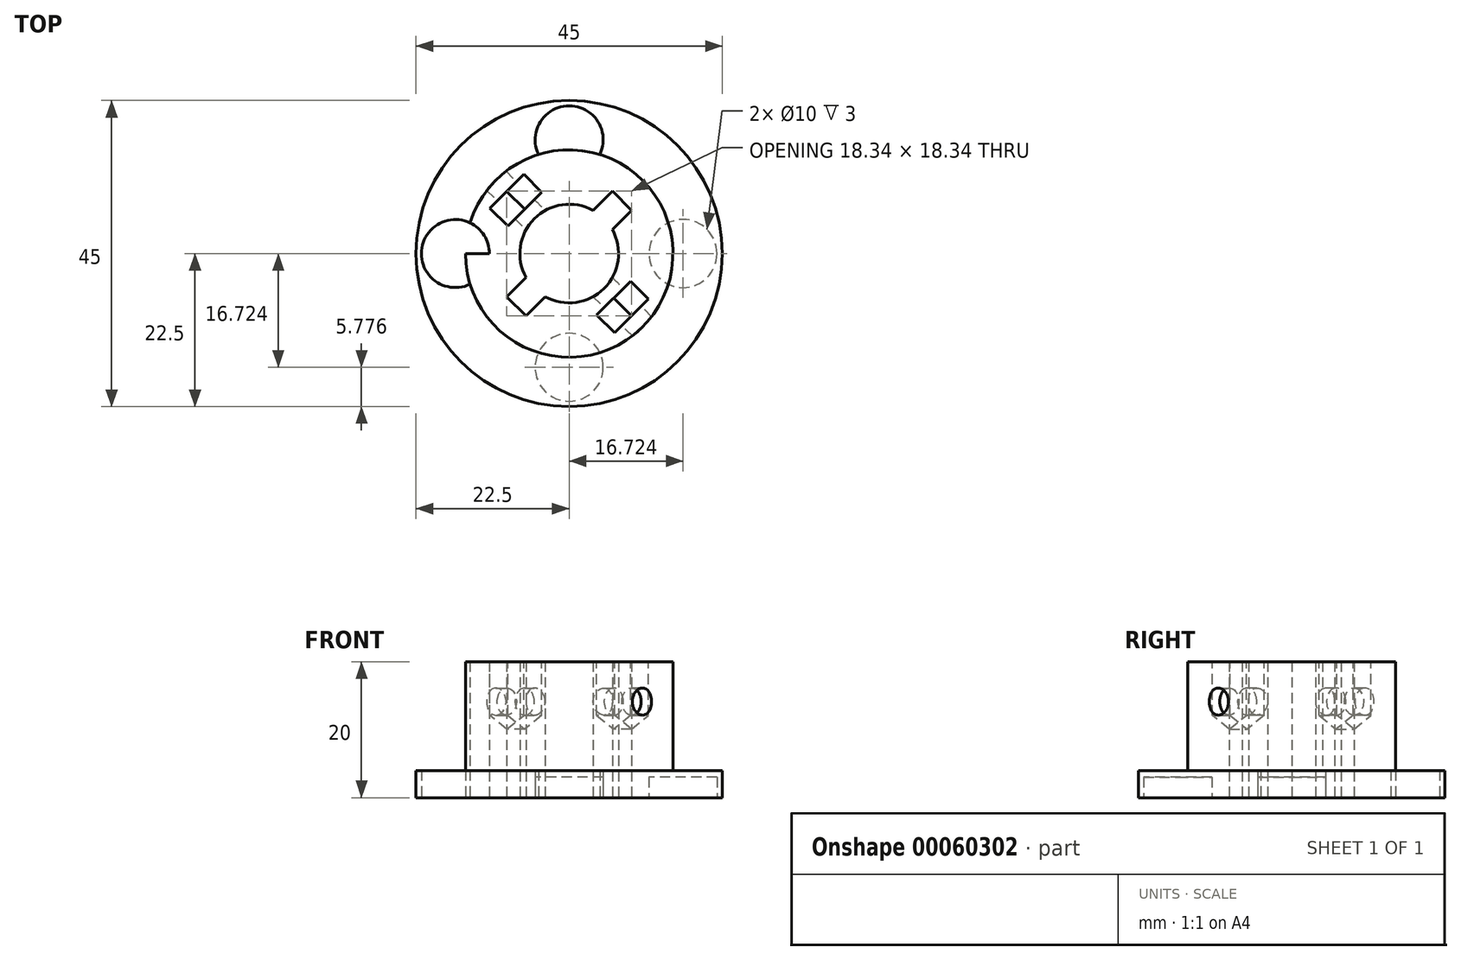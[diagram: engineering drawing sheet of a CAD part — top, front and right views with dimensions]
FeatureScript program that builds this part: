
annotation { "Feature Type Name" : "Feature", "Feature Type Description" : "" }
export const myFeature = defineFeature(function(context is Context, id is Id, definition is map)
    precondition{}
    {
        {
            var Q0;
            Q0=qCreatedBy(makeId("Top.planeOp"),FACE);
            var sketch = newSketch(context, id + "F0", { "sketchPlane" : qUnion([Q0])});
            skCircle(sketch, "E0", {"center": v(0, 0) * mm, "radius": 22.5 * mm});
            skLineSegment(sketch, "E1", {"start": v(0, 22.5) * mm, "end": v(0, -22.5) * mm});
            skLineSegment(sketch, "E2", {"start": v(-22.5, 0) * mm, "end": v(22.5, 0) * mm});
            skCircle(sketch, "E3", {"center": v(0, 0) * mm, "radius": 7.25 * mm});
            skCircle(sketch, "E4", {"center": v(0, 0) * mm, "radius": 15.25 * mm});
            skCircle(sketch, "E5", {"center": v(0, -16.72) * mm, "radius": 5 * mm});
            skLineSegment(sketch, "E6", {"start": v(-15.9, -15.9) * mm, "end": v(15.9, 15.9) * mm});
            skCircle(sketch, "E7.MirrorC", {"center": v(0, 16.72) * mm, "radius": 5 * mm});
            skCircle(sketch, "E8.MirrorC", {"center": v(-16.72, 0) * mm, "radius": 5 * mm});
            skCircle(sketch, "E9.MirrorC", {"center": v(16.72, 0) * mm, "radius": 5 * mm});
            skLineSegment(sketch, "E10", {"start": v(-6.34, -3.51) * mm, "end": v(-9.17, -6.34) * mm});
            skLineSegment(sketch, "E11", {"start": v(-9.17, -6.34) * mm, "end": v(-6.34, -9.17) * mm});
            skLineSegment(sketch, "E12", {"start": v(-6.34, -9.17) * mm, "end": v(-3.51, -6.34) * mm});
            skLineSegment(sketch, "E13", {"start": v(-15.9, 15.9) * mm, "end": v(15.9, -15.9) * mm, "construction": true});
            skLineSegment(sketch, "E14.MirrorCS", {"start": v(3.51, 6.34) * mm, "end": v(6.34, 9.17) * mm});
            skLineSegment(sketch, "E15.MirrorCS", {"start": v(6.34, 9.17) * mm, "end": v(9.17, 6.34) * mm});
            skLineSegment(sketch, "E16.MirrorCS", {"start": v(9.17, 6.34) * mm, "end": v(6.34, 3.51) * mm});
            skSolve(sketch);
        }
        {
            var Q0;
            {var subQ0=sQuery(id+"F0.wireOp",EDGE,"E4");var subQ1=sQuery(id+"F0.wireOp",EDGE,"E1");var subQ2=makeQuery(id+"F0.imprint","INTERSECT",VERTEX,{"disambiguationData":[OD(0.0)],"derivedFrom":[subQ1,subQ0]});Q0=makeQuery(id+"F0.imprint","IMPRINT",FACE,{"disambiguationData":[TD([[makeQuery(id+"F0.imprint","IMPRINT",EDGE,{"disambiguationData":[TD([[subQ2,-1.0]])],"derivedFrom":subQ1}),-1.0]])]});}
            var Q1;
            {var subQ0=sQuery(id+"F0.wireOp",EDGE,"E4");var subQ1=sQuery(id+"F0.wireOp",EDGE,"E1");var subQ2=makeQuery(id+"F0.imprint","INTERSECT",VERTEX,{"disambiguationData":[OD(0.0)],"derivedFrom":[subQ1,subQ0]});Q1=makeQuery(id+"F0.imprint","IMPRINT",FACE,{"disambiguationData":[TD([[makeQuery(id+"F0.imprint","IMPRINT",EDGE,{"disambiguationData":[TD([[subQ2,-1.0]])],"derivedFrom":subQ1}),1.0]])]});}
            var Q2;
            {var subQ5=sQuery(id+"F0.wireOp",EDGE,"E2");var subQ8=sQuery(id+"F0.wireOp",EDGE,"E3");var subQ9=makeQuery(id+"F0.imprint","INTERSECT",VERTEX,{"disambiguationData":[OD(1.0)],"derivedFrom":[subQ5,subQ8]});Q2=makeQuery(id+"F0.imprint","IMPRINT",FACE,{"disambiguationData":[TD([[makeQuery(id+"F0.imprint","IMPRINT",EDGE,{"disambiguationData":[TD([[subQ9,-1.0]])],"derivedFrom":subQ5}),1.0]])]});}
            var Q3;
            {var subQ0=sQuery(id+"F0.wireOp",EDGE,"E3");var subQ1=sQuery(id+"F0.wireOp",EDGE,"E1");var subQ2=makeQuery(id+"F0.imprint","INTERSECT",VERTEX,{"disambiguationData":[OD(1.0)],"derivedFrom":[subQ1,subQ0]});Q3=makeQuery(id+"F0.imprint","IMPRINT",FACE,{"disambiguationData":[TD([[makeQuery(id+"F0.imprint","IMPRINT",EDGE,{"disambiguationData":[TD([[subQ2,-1.0]])],"derivedFrom":subQ1}),1.0]])]});}
            var Q4;
            {var subQ6=sQuery(id+"F0.wireOp",EDGE,"E3");var subQ7=sQuery(id+"F0.wireOp",EDGE,"E1");var subQ8=makeQuery(id+"F0.imprint","INTERSECT",VERTEX,{"disambiguationData":[OD(1.0)],"derivedFrom":[subQ7,subQ6]});Q4=makeQuery(id+"F0.imprint","IMPRINT",FACE,{"disambiguationData":[TD([[makeQuery(id+"F0.imprint","IMPRINT",EDGE,{"disambiguationData":[TD([[subQ8,-1.0]])],"derivedFrom":subQ7}),-1.0]])]});}
            var Q5;
            {var subQ1=sQuery(id+"F0.wireOp",EDGE,"E4");var subQ5=sQuery(id+"F0.wireOp",EDGE,"E2");var subQ6=makeQuery(id+"F0.imprint","INTERSECT",VERTEX,{"disambiguationData":[OD(0.0)],"derivedFrom":[subQ5,subQ1]});Q5=makeQuery(id+"F0.imprint","IMPRINT",FACE,{"disambiguationData":[TD([[makeQuery(id+"F0.imprint","IMPRINT",EDGE,{"disambiguationData":[TD([[subQ6,-1.0]])],"derivedFrom":subQ5}),-1.0]])]});}
            var Q6;
            {var subQ0=sQuery(id+"F0.wireOp",EDGE,"1c631775-3706-4f81-9fae-aeb5620db3840.MirrorC");var subQ1=sQuery(id+"F0.wireOp",EDGE,"E4");var subQ2=makeQuery(id+"F0.imprint","INTERSECT",VERTEX,{"disambiguationData":[OD(0.0)],"derivedFrom":[subQ1,subQ0]});Q6=makeQuery(id+"F0.imprint","IMPRINT",FACE,{"disambiguationData":[TD([[makeQuery(id+"F0.imprint","IMPRINT",EDGE,{"disambiguationData":[TD([[subQ2,-1.0]])],"derivedFrom":subQ1}),1.0]])]});}
            var Q7;
            {var subQ0=sQuery(id+"F0.wireOp",EDGE,"60ae7ea0-6620-475c-871b-af027508dd5f0.MirrorC");var subQ1=sQuery(id+"F0.wireOp",EDGE,"E4");var subQ2=makeQuery(id+"F0.imprint","INTERSECT",VERTEX,{"disambiguationData":[OD(0.0)],"derivedFrom":[subQ1,subQ0]});Q7=makeQuery(id+"F0.imprint","IMPRINT",FACE,{"disambiguationData":[TD([[makeQuery(id+"F0.imprint","IMPRINT",EDGE,{"disambiguationData":[TD([[subQ2,-1.0]])],"derivedFrom":subQ1}),1.0]])]});}
            var Q8;
            {var subQ0=sQuery(id+"F0.wireOp",EDGE,"c14ca91b-31c8-40ef-a71a-b8f91e1f63390.MirrorC");var subQ1=sQuery(id+"F0.wireOp",EDGE,"E4");var subQ2=makeQuery(id+"F0.imprint","INTERSECT",VERTEX,{"disambiguationData":[OD(0.0)],"derivedFrom":[subQ1,subQ0]});Q8=makeQuery(id+"F0.imprint","IMPRINT",FACE,{"disambiguationData":[TD([[makeQuery(id+"F0.imprint","IMPRINT",EDGE,{"disambiguationData":[TD([[subQ2,-1.0]])],"derivedFrom":subQ1}),1.0]])]});}
            var Q9;
            {var subQ0=sQuery(id+"F0.wireOp",EDGE,"be21c227-3566-4778-a96a-078e8c0b7c8a0.MirrorC");var subQ1=sQuery(id+"F0.wireOp",EDGE,"E4");var subQ2=makeQuery(id+"F0.imprint","INTERSECT",VERTEX,{"disambiguationData":[OD(0.0)],"derivedFrom":[subQ1,subQ0]});Q9=makeQuery(id+"F0.imprint","IMPRINT",FACE,{"disambiguationData":[TD([[makeQuery(id+"F0.imprint","IMPRINT",EDGE,{"disambiguationData":[TD([[subQ2,-1.0]])],"derivedFrom":subQ1}),1.0]])]});}
            var Q10;
            {var subQ0=sQuery(id+"F0.wireOp",EDGE,"ab68310c-7daf-4449-9c12-ef71371e41db0.MirrorC");var subQ1=sQuery(id+"F0.wireOp",EDGE,"E4");var subQ2=makeQuery(id+"F0.imprint","INTERSECT",VERTEX,{"disambiguationData":[OD(0.0)],"derivedFrom":[subQ1,subQ0]});Q10=makeQuery(id+"F0.imprint","IMPRINT",FACE,{"disambiguationData":[TD([[makeQuery(id+"F0.imprint","IMPRINT",EDGE,{"disambiguationData":[TD([[subQ2,-1.0]])],"derivedFrom":subQ1}),1.0]])]});}
            var Q11;
            {var subQ0=sQuery(id+"F0.wireOp",EDGE,"E5");var subQ1=sQuery(id+"F0.wireOp",EDGE,"E4");var subQ2=makeQuery(id+"F0.imprint","INTERSECT",VERTEX,{"disambiguationData":[OD(0.0)],"derivedFrom":[subQ1,subQ0]});Q11=makeQuery(id+"F0.imprint","IMPRINT",FACE,{"disambiguationData":[TD([[makeQuery(id+"F0.imprint","IMPRINT",EDGE,{"disambiguationData":[TD([[subQ2,-1.0]])],"derivedFrom":subQ1}),1.0]])]});}
            var Q12;
            {var subQ0=sQuery(id+"F0.wireOp",EDGE,"a2d47717-2f6c-4d2c-92b3-d8f29983befe0.MirrorC");var subQ1=sQuery(id+"F0.wireOp",EDGE,"E4");var subQ2=makeQuery(id+"F0.imprint","INTERSECT",VERTEX,{"disambiguationData":[OD(0.0)],"derivedFrom":[subQ1,subQ0]});Q12=makeQuery(id+"F0.imprint","IMPRINT",FACE,{"disambiguationData":[TD([[makeQuery(id+"F0.imprint","IMPRINT",EDGE,{"disambiguationData":[TD([[subQ2,-1.0]])],"derivedFrom":subQ1}),1.0]])]});}
            var Q13;
            {var subQ0=sQuery(id+"F0.wireOp",EDGE,"ad0277b0-81cc-4cec-893f-fa6e84c42cf90.MirrorC");var subQ1=sQuery(id+"F0.wireOp",EDGE,"E4");var subQ2=makeQuery(id+"F0.imprint","INTERSECT",VERTEX,{"disambiguationData":[OD(0.0)],"derivedFrom":[subQ1,subQ0]});Q13=makeQuery(id+"F0.imprint","IMPRINT",FACE,{"disambiguationData":[TD([[makeQuery(id+"F0.imprint","IMPRINT",EDGE,{"disambiguationData":[TD([[subQ2,-1.0]])],"derivedFrom":subQ1}),1.0]])]});}
            var Q14;
            {var subQ0=sQuery(id+"F0.wireOp",EDGE,"E8.MirrorC");var subQ6=sQuery(id+"F0.wireOp",EDGE,"E2");var subQ9=makeQuery(id+"F0.imprint","INTERSECT",VERTEX,{"disambiguationData":[OD(1.0)],"derivedFrom":[subQ6,subQ0]});Q14=makeQuery(id+"F0.imprint","IMPRINT",FACE,{"disambiguationData":[TD([[makeQuery(id+"F0.imprint","IMPRINT",EDGE,{"disambiguationData":[TD([[subQ9,-1.0]])],"derivedFrom":subQ6}),-1.0]])]});}
            var Q15;
            {var subQ0=sQuery(id+"F0.wireOp",EDGE,"E5");var subQ1=sQuery(id+"F0.wireOp",EDGE,"E1");var subQ2=makeQuery(id+"F0.imprint","INTERSECT",VERTEX,{"disambiguationData":[OD(0.0)],"derivedFrom":[subQ1,subQ0]});Q15=makeQuery(id+"F0.imprint","IMPRINT",FACE,{"disambiguationData":[TD([[makeQuery(id+"F0.imprint","IMPRINT",EDGE,{"disambiguationData":[TD([[subQ2,-1.0]])],"derivedFrom":subQ1}),1.0]])]});}
            var Q16;
            {var subQ1=sQuery(id+"F0.wireOp",EDGE,"E1");var subQ5=sQuery(id+"F0.wireOp",EDGE,"E7.MirrorC");var subQ11=makeQuery(id+"F0.imprint","INTERSECT",VERTEX,{"disambiguationData":[OD(1.0)],"derivedFrom":[subQ1,subQ5]});Q16=makeQuery(id+"F0.imprint","IMPRINT",FACE,{"disambiguationData":[TD([[makeQuery(id+"F0.imprint","IMPRINT",EDGE,{"disambiguationData":[TD([[subQ11,-1.0]])],"derivedFrom":subQ1}),-1.0]])]});}
            var Q17;
            {var subQ5=sQuery(id+"F0.wireOp",EDGE,"E7.MirrorC");var subQ6=sQuery(id+"F0.wireOp",EDGE,"E1");var subQ7=makeQuery(id+"F0.imprint","INTERSECT",VERTEX,{"disambiguationData":[OD(1.0)],"derivedFrom":[subQ6,subQ5]});Q17=makeQuery(id+"F0.imprint","IMPRINT",FACE,{"disambiguationData":[TD([[makeQuery(id+"F0.imprint","IMPRINT",EDGE,{"disambiguationData":[TD([[subQ7,-1.0]])],"derivedFrom":subQ6}),1.0]])]});}
            var Q18;
            {var subQ0=sQuery(id+"F0.wireOp",EDGE,"E9.MirrorC");var subQ1=sQuery(id+"F0.wireOp",EDGE,"E2");var subQ2=makeQuery(id+"F0.imprint","INTERSECT",VERTEX,{"disambiguationData":[OD(0.0)],"derivedFrom":[subQ1,subQ0]});Q18=makeQuery(id+"F0.imprint","IMPRINT",FACE,{"disambiguationData":[TD([[makeQuery(id+"F0.imprint","IMPRINT",EDGE,{"disambiguationData":[TD([[subQ2,-1.0]])],"derivedFrom":subQ1}),1.0]])]});}
            var Q19;
            {var subQ0=sQuery(id+"F0.wireOp",EDGE,"E9.MirrorC");var subQ1=sQuery(id+"F0.wireOp",EDGE,"E2");var subQ2=makeQuery(id+"F0.imprint","INTERSECT",VERTEX,{"disambiguationData":[OD(0.0)],"derivedFrom":[subQ1,subQ0]});Q19=makeQuery(id+"F0.imprint","IMPRINT",FACE,{"disambiguationData":[TD([[makeQuery(id+"F0.imprint","IMPRINT",EDGE,{"disambiguationData":[TD([[subQ2,-1.0]])],"derivedFrom":subQ1}),-1.0]])]});}
            extrude(context, id + "F1", {"entities" : qUnion([Q0, Q1, Q2, Q3, Q4, Q5, Q6, Q7, Q8, Q9, Q10, Q11, Q12, Q13, Q14, Q15, Q16, Q17, Q18, Q19]), "depth" : 20 * mm});
        }
        {
            var Q0;
            {var subQ1=sQuery(id+"F0.wireOp",EDGE,"E0");var subQ5=sQuery(id+"F0.wireOp",EDGE,"E1");var subQ9=makeQuery(id+"F0.imprint","INTERSECT",VERTEX,{"disambiguationData":[OD(1.0)],"derivedFrom":[subQ1,subQ5]});Q0=makeQuery(id+"F0.imprint","IMPRINT",FACE,{"disambiguationData":[TD([[makeQuery(id+"F0.imprint","IMPRINT",EDGE,{"disambiguationData":[TD([[subQ9,-1.0]])],"derivedFrom":subQ1}),1.0]])]});}
            var Q1;
            {var subQ0=sQuery(id+"F0.wireOp",EDGE,"ab68310c-7daf-4449-9c12-ef71371e41db0.MirrorC");var subQ1=sQuery(id+"F0.wireOp",EDGE,"E4");var subQ2=makeQuery(id+"F0.imprint","INTERSECT",VERTEX,{"disambiguationData":[OD(0.0)],"derivedFrom":[subQ1,subQ0]});Q1=makeQuery(id+"F0.imprint","IMPRINT",FACE,{"disambiguationData":[TD([[makeQuery(id+"F0.imprint","IMPRINT",EDGE,{"disambiguationData":[TD([[subQ2,-1.0]])],"derivedFrom":subQ1}),-1.0]])]});}
            var Q2;
            {var subQ5=sQuery(id+"F0.wireOp",EDGE,"E2");var subQ8=sQuery(id+"F0.wireOp",EDGE,"E0");var subQ9=makeQuery(id+"F0.imprint","INTERSECT",VERTEX,{"disambiguationData":[OD(1.0)],"derivedFrom":[subQ8,subQ5]});Q2=makeQuery(id+"F0.imprint","IMPRINT",FACE,{"disambiguationData":[TD([[makeQuery(id+"F0.imprint","IMPRINT",EDGE,{"disambiguationData":[TD([[subQ9,-1.0]])],"derivedFrom":subQ8}),1.0]])]});}
            var Q3;
            {var subQ0=sQuery(id+"F0.wireOp",EDGE,"be21c227-3566-4778-a96a-078e8c0b7c8a0.MirrorC");var subQ1=sQuery(id+"F0.wireOp",EDGE,"E4");var subQ2=makeQuery(id+"F0.imprint","INTERSECT",VERTEX,{"disambiguationData":[OD(0.0)],"derivedFrom":[subQ1,subQ0]});Q3=makeQuery(id+"F0.imprint","IMPRINT",FACE,{"disambiguationData":[TD([[makeQuery(id+"F0.imprint","IMPRINT",EDGE,{"disambiguationData":[TD([[subQ2,-1.0]])],"derivedFrom":subQ1}),-1.0]])]});}
            var Q4;
            {var subQ0=sQuery(id+"F0.wireOp",EDGE,"E5");var subQ1=sQuery(id+"F0.wireOp",EDGE,"E4");var subQ2=makeQuery(id+"F0.imprint","INTERSECT",VERTEX,{"disambiguationData":[OD(0.0)],"derivedFrom":[subQ1,subQ0]});Q4=makeQuery(id+"F0.imprint","IMPRINT",FACE,{"disambiguationData":[TD([[makeQuery(id+"F0.imprint","IMPRINT",EDGE,{"disambiguationData":[TD([[subQ2,-1.0]])],"derivedFrom":subQ1}),-1.0]])]});}
            var Q5;
            {var subQ5=sQuery(id+"F0.wireOp",EDGE,"E1");var subQ8=sQuery(id+"F0.wireOp",EDGE,"E0");var subQ10=makeQuery(id+"F0.imprint","INTERSECT",VERTEX,{"disambiguationData":[OD(1.0)],"derivedFrom":[subQ8,subQ5]});Q5=makeQuery(id+"F0.imprint","IMPRINT",FACE,{"disambiguationData":[TD([[makeQuery(id+"F0.imprint","IMPRINT",EDGE,{"disambiguationData":[TD([[subQ10,1.0]])],"derivedFrom":subQ8}),1.0]])]});}
            var Q6;
            {var subQ0=sQuery(id+"F0.wireOp",EDGE,"a2d47717-2f6c-4d2c-92b3-d8f29983befe0.MirrorC");var subQ1=sQuery(id+"F0.wireOp",EDGE,"E4");var subQ2=makeQuery(id+"F0.imprint","INTERSECT",VERTEX,{"disambiguationData":[OD(0.0)],"derivedFrom":[subQ1,subQ0]});Q6=makeQuery(id+"F0.imprint","IMPRINT",FACE,{"disambiguationData":[TD([[makeQuery(id+"F0.imprint","IMPRINT",EDGE,{"disambiguationData":[TD([[subQ2,-1.0]])],"derivedFrom":subQ1}),-1.0]])]});}
            var Q7;
            {var subQ5=sQuery(id+"F0.wireOp",EDGE,"E2");var subQ8=sQuery(id+"F0.wireOp",EDGE,"E0");var subQ9=makeQuery(id+"F0.imprint","INTERSECT",VERTEX,{"disambiguationData":[OD(0.0)],"derivedFrom":[subQ8,subQ5]});Q7=makeQuery(id+"F0.imprint","IMPRINT",FACE,{"disambiguationData":[TD([[makeQuery(id+"F0.imprint","IMPRINT",EDGE,{"disambiguationData":[TD([[subQ9,-1.0]])],"derivedFrom":subQ8}),1.0]])]});}
            var Q8;
            {var subQ0=sQuery(id+"F0.wireOp",EDGE,"ad0277b0-81cc-4cec-893f-fa6e84c42cf90.MirrorC");var subQ1=sQuery(id+"F0.wireOp",EDGE,"E4");var subQ2=makeQuery(id+"F0.imprint","INTERSECT",VERTEX,{"disambiguationData":[OD(0.0)],"derivedFrom":[subQ1,subQ0]});Q8=makeQuery(id+"F0.imprint","IMPRINT",FACE,{"disambiguationData":[TD([[makeQuery(id+"F0.imprint","IMPRINT",EDGE,{"disambiguationData":[TD([[subQ2,-1.0]])],"derivedFrom":subQ1}),-1.0]])]});}
            var Q9;
            {var subQ0=sQuery(id+"F0.wireOp",EDGE,"1c631775-3706-4f81-9fae-aeb5620db3840.MirrorC");var subQ1=sQuery(id+"F0.wireOp",EDGE,"E4");var subQ2=makeQuery(id+"F0.imprint","INTERSECT",VERTEX,{"disambiguationData":[OD(0.0)],"derivedFrom":[subQ1,subQ0]});Q9=makeQuery(id+"F0.imprint","IMPRINT",FACE,{"disambiguationData":[TD([[makeQuery(id+"F0.imprint","IMPRINT",EDGE,{"disambiguationData":[TD([[subQ2,-1.0]])],"derivedFrom":subQ1}),-1.0]])]});}
            var Q10;
            {var subQ1=sQuery(id+"F0.wireOp",EDGE,"E1");var subQ6=sQuery(id+"F0.wireOp",EDGE,"E0");var subQ9=makeQuery(id+"F0.imprint","INTERSECT",VERTEX,{"disambiguationData":[OD(0.0)],"derivedFrom":[subQ6,subQ1]});Q10=makeQuery(id+"F0.imprint","IMPRINT",FACE,{"disambiguationData":[TD([[makeQuery(id+"F0.imprint","IMPRINT",EDGE,{"disambiguationData":[TD([[subQ9,-1.0]])],"derivedFrom":subQ6}),1.0]])]});}
            var Q11;
            {var subQ0=sQuery(id+"F0.wireOp",EDGE,"60ae7ea0-6620-475c-871b-af027508dd5f0.MirrorC");var subQ1=sQuery(id+"F0.wireOp",EDGE,"E4");var subQ2=makeQuery(id+"F0.imprint","INTERSECT",VERTEX,{"disambiguationData":[OD(0.0)],"derivedFrom":[subQ1,subQ0]});Q11=makeQuery(id+"F0.imprint","IMPRINT",FACE,{"disambiguationData":[TD([[makeQuery(id+"F0.imprint","IMPRINT",EDGE,{"disambiguationData":[TD([[subQ2,-1.0]])],"derivedFrom":subQ1}),-1.0]])]});}
            var Q12;
            {var subQ0=sQuery(id+"F0.wireOp",EDGE,"c14ca91b-31c8-40ef-a71a-b8f91e1f63390.MirrorC");var subQ1=sQuery(id+"F0.wireOp",EDGE,"E4");var subQ2=makeQuery(id+"F0.imprint","INTERSECT",VERTEX,{"disambiguationData":[OD(0.0)],"derivedFrom":[subQ1,subQ0]});Q12=makeQuery(id+"F0.imprint","IMPRINT",FACE,{"disambiguationData":[TD([[makeQuery(id+"F0.imprint","IMPRINT",EDGE,{"disambiguationData":[TD([[subQ2,-1.0]])],"derivedFrom":subQ1}),-1.0]])]});}
            var Q13;
            {var subQ1=sQuery(id+"F0.wireOp",EDGE,"E1");var subQ8=sQuery(id+"F0.wireOp",EDGE,"E0");var subQ9=makeQuery(id+"F0.imprint","INTERSECT",VERTEX,{"disambiguationData":[OD(0.0)],"derivedFrom":[subQ8,subQ1]});Q13=makeQuery(id+"F0.imprint","IMPRINT",FACE,{"disambiguationData":[TD([[makeQuery(id+"F0.imprint","IMPRINT",EDGE,{"disambiguationData":[TD([[subQ9,1.0]])],"derivedFrom":subQ8}),1.0]])]});}
            var Q14;
            {var subQ0=sQuery(id+"F0.wireOp",EDGE,"E4");var subQ1=sQuery(id+"F0.wireOp",EDGE,"E1");var subQ2=makeQuery(id+"F0.imprint","INTERSECT",VERTEX,{"disambiguationData":[OD(1.0)],"derivedFrom":[subQ1,subQ0]});Q14=makeQuery(id+"F0.imprint","IMPRINT",FACE,{"disambiguationData":[TD([[makeQuery(id+"F0.imprint","IMPRINT",EDGE,{"disambiguationData":[TD([[subQ2,-1.0]])],"derivedFrom":subQ1}),1.0]])]});}
            var Q15;
            {var subQ0=sQuery(id+"F0.wireOp",EDGE,"E4");var subQ1=sQuery(id+"F0.wireOp",EDGE,"E2");var subQ2=makeQuery(id+"F0.imprint","INTERSECT",VERTEX,{"disambiguationData":[OD(1.0)],"derivedFrom":[subQ1,subQ0]});Q15=makeQuery(id+"F0.imprint","IMPRINT",FACE,{"disambiguationData":[TD([[makeQuery(id+"F0.imprint","IMPRINT",EDGE,{"disambiguationData":[TD([[subQ2,-1.0]])],"derivedFrom":subQ1}),-1.0]])]});}
            var Q16;
            {var subQ0=sQuery(id+"F0.wireOp",EDGE,"E4");var subQ1=sQuery(id+"F0.wireOp",EDGE,"E2");var subQ2=makeQuery(id+"F0.imprint","INTERSECT",VERTEX,{"disambiguationData":[OD(1.0)],"derivedFrom":[subQ1,subQ0]});Q16=makeQuery(id+"F0.imprint","IMPRINT",FACE,{"disambiguationData":[TD([[makeQuery(id+"F0.imprint","IMPRINT",EDGE,{"disambiguationData":[TD([[subQ2,-1.0]])],"derivedFrom":subQ1}),1.0]])]});}
            extrude(context, id + "F2", {"entities" : qUnion([Q0, Q1, Q2, Q3, Q4, Q5, Q6, Q7, Q8, Q9, Q10, Q11, Q12, Q13, Q14, Q15, Q16]), "operationType" : NewBodyOperationType.ADD, "depth" : 4 * mm});
        }
        {
            var Q0;
            {var subQ0=sQuery(id+"F0.wireOp",EDGE,"ad0277b0-81cc-4cec-893f-fa6e84c42cf90.MirrorC");var subQ1=sQuery(id+"F0.wireOp",EDGE,"E4");var subQ2=makeQuery(id+"F0.imprint","INTERSECT",VERTEX,{"disambiguationData":[OD(0.0)],"derivedFrom":[subQ1,subQ0]});Q0=makeQuery(id+"F0.imprint","IMPRINT",FACE,{"disambiguationData":[TD([[makeQuery(id+"F0.imprint","IMPRINT",EDGE,{"disambiguationData":[TD([[subQ2,-1.0]])],"derivedFrom":subQ1}),-1.0]])]});}
            var Q1;
            {var subQ0=sQuery(id+"F0.wireOp",EDGE,"ad0277b0-81cc-4cec-893f-fa6e84c42cf90.MirrorC");var subQ1=sQuery(id+"F0.wireOp",EDGE,"E4");var subQ2=makeQuery(id+"F0.imprint","INTERSECT",VERTEX,{"disambiguationData":[OD(0.0)],"derivedFrom":[subQ1,subQ0]});Q1=makeQuery(id+"F0.imprint","IMPRINT",FACE,{"disambiguationData":[TD([[makeQuery(id+"F0.imprint","IMPRINT",EDGE,{"disambiguationData":[TD([[subQ2,-1.0]])],"derivedFrom":subQ1}),1.0]])]});}
            var Q2;
            {var subQ0=sQuery(id+"F0.wireOp",EDGE,"a2d47717-2f6c-4d2c-92b3-d8f29983befe0.MirrorC");var subQ1=sQuery(id+"F0.wireOp",EDGE,"E4");var subQ2=makeQuery(id+"F0.imprint","INTERSECT",VERTEX,{"disambiguationData":[OD(0.0)],"derivedFrom":[subQ1,subQ0]});Q2=makeQuery(id+"F0.imprint","IMPRINT",FACE,{"disambiguationData":[TD([[makeQuery(id+"F0.imprint","IMPRINT",EDGE,{"disambiguationData":[TD([[subQ2,-1.0]])],"derivedFrom":subQ1}),-1.0]])]});}
            var Q3;
            {var subQ0=sQuery(id+"F0.wireOp",EDGE,"a2d47717-2f6c-4d2c-92b3-d8f29983befe0.MirrorC");var subQ1=sQuery(id+"F0.wireOp",EDGE,"E4");var subQ2=makeQuery(id+"F0.imprint","INTERSECT",VERTEX,{"disambiguationData":[OD(0.0)],"derivedFrom":[subQ1,subQ0]});Q3=makeQuery(id+"F0.imprint","IMPRINT",FACE,{"disambiguationData":[TD([[makeQuery(id+"F0.imprint","IMPRINT",EDGE,{"disambiguationData":[TD([[subQ2,-1.0]])],"derivedFrom":subQ1}),1.0]])]});}
            var Q4;
            {var subQ0=sQuery(id+"F0.wireOp",EDGE,"E5");var subQ1=sQuery(id+"F0.wireOp",EDGE,"E4");var subQ2=makeQuery(id+"F0.imprint","INTERSECT",VERTEX,{"disambiguationData":[OD(0.0)],"derivedFrom":[subQ1,subQ0]});Q4=makeQuery(id+"F0.imprint","IMPRINT",FACE,{"disambiguationData":[TD([[makeQuery(id+"F0.imprint","IMPRINT",EDGE,{"disambiguationData":[TD([[subQ2,-1.0]])],"derivedFrom":subQ1}),-1.0]])]});}
            var Q5;
            {var subQ0=sQuery(id+"F0.wireOp",EDGE,"E5");var subQ1=sQuery(id+"F0.wireOp",EDGE,"E4");var subQ2=makeQuery(id+"F0.imprint","INTERSECT",VERTEX,{"disambiguationData":[OD(0.0)],"derivedFrom":[subQ1,subQ0]});Q5=makeQuery(id+"F0.imprint","IMPRINT",FACE,{"disambiguationData":[TD([[makeQuery(id+"F0.imprint","IMPRINT",EDGE,{"disambiguationData":[TD([[subQ2,-1.0]])],"derivedFrom":subQ1}),1.0]])]});}
            var Q6;
            {var subQ0=sQuery(id+"F0.wireOp",EDGE,"ab68310c-7daf-4449-9c12-ef71371e41db0.MirrorC");var subQ1=sQuery(id+"F0.wireOp",EDGE,"E4");var subQ2=makeQuery(id+"F0.imprint","INTERSECT",VERTEX,{"disambiguationData":[OD(0.0)],"derivedFrom":[subQ1,subQ0]});Q6=makeQuery(id+"F0.imprint","IMPRINT",FACE,{"disambiguationData":[TD([[makeQuery(id+"F0.imprint","IMPRINT",EDGE,{"disambiguationData":[TD([[subQ2,-1.0]])],"derivedFrom":subQ1}),-1.0]])]});}
            var Q7;
            {var subQ0=sQuery(id+"F0.wireOp",EDGE,"ab68310c-7daf-4449-9c12-ef71371e41db0.MirrorC");var subQ1=sQuery(id+"F0.wireOp",EDGE,"E4");var subQ2=makeQuery(id+"F0.imprint","INTERSECT",VERTEX,{"disambiguationData":[OD(0.0)],"derivedFrom":[subQ1,subQ0]});Q7=makeQuery(id+"F0.imprint","IMPRINT",FACE,{"disambiguationData":[TD([[makeQuery(id+"F0.imprint","IMPRINT",EDGE,{"disambiguationData":[TD([[subQ2,-1.0]])],"derivedFrom":subQ1}),1.0]])]});}
            var Q8;
            {var subQ0=sQuery(id+"F0.wireOp",EDGE,"be21c227-3566-4778-a96a-078e8c0b7c8a0.MirrorC");var subQ1=sQuery(id+"F0.wireOp",EDGE,"E4");var subQ2=makeQuery(id+"F0.imprint","INTERSECT",VERTEX,{"disambiguationData":[OD(0.0)],"derivedFrom":[subQ1,subQ0]});Q8=makeQuery(id+"F0.imprint","IMPRINT",FACE,{"disambiguationData":[TD([[makeQuery(id+"F0.imprint","IMPRINT",EDGE,{"disambiguationData":[TD([[subQ2,-1.0]])],"derivedFrom":subQ1}),-1.0]])]});}
            var Q9;
            {var subQ0=sQuery(id+"F0.wireOp",EDGE,"be21c227-3566-4778-a96a-078e8c0b7c8a0.MirrorC");var subQ1=sQuery(id+"F0.wireOp",EDGE,"E4");var subQ2=makeQuery(id+"F0.imprint","INTERSECT",VERTEX,{"disambiguationData":[OD(0.0)],"derivedFrom":[subQ1,subQ0]});Q9=makeQuery(id+"F0.imprint","IMPRINT",FACE,{"disambiguationData":[TD([[makeQuery(id+"F0.imprint","IMPRINT",EDGE,{"disambiguationData":[TD([[subQ2,-1.0]])],"derivedFrom":subQ1}),1.0]])]});}
            var Q10;
            {var subQ0=sQuery(id+"F0.wireOp",EDGE,"c14ca91b-31c8-40ef-a71a-b8f91e1f63390.MirrorC");var subQ1=sQuery(id+"F0.wireOp",EDGE,"E4");var subQ2=makeQuery(id+"F0.imprint","INTERSECT",VERTEX,{"disambiguationData":[OD(0.0)],"derivedFrom":[subQ1,subQ0]});Q10=makeQuery(id+"F0.imprint","IMPRINT",FACE,{"disambiguationData":[TD([[makeQuery(id+"F0.imprint","IMPRINT",EDGE,{"disambiguationData":[TD([[subQ2,-1.0]])],"derivedFrom":subQ1}),-1.0]])]});}
            var Q11;
            {var subQ0=sQuery(id+"F0.wireOp",EDGE,"c14ca91b-31c8-40ef-a71a-b8f91e1f63390.MirrorC");var subQ1=sQuery(id+"F0.wireOp",EDGE,"E4");var subQ2=makeQuery(id+"F0.imprint","INTERSECT",VERTEX,{"disambiguationData":[OD(0.0)],"derivedFrom":[subQ1,subQ0]});Q11=makeQuery(id+"F0.imprint","IMPRINT",FACE,{"disambiguationData":[TD([[makeQuery(id+"F0.imprint","IMPRINT",EDGE,{"disambiguationData":[TD([[subQ2,-1.0]])],"derivedFrom":subQ1}),1.0]])]});}
            var Q12;
            {var subQ0=sQuery(id+"F0.wireOp",EDGE,"60ae7ea0-6620-475c-871b-af027508dd5f0.MirrorC");var subQ1=sQuery(id+"F0.wireOp",EDGE,"E4");var subQ2=makeQuery(id+"F0.imprint","INTERSECT",VERTEX,{"disambiguationData":[OD(0.0)],"derivedFrom":[subQ1,subQ0]});Q12=makeQuery(id+"F0.imprint","IMPRINT",FACE,{"disambiguationData":[TD([[makeQuery(id+"F0.imprint","IMPRINT",EDGE,{"disambiguationData":[TD([[subQ2,-1.0]])],"derivedFrom":subQ1}),-1.0]])]});}
            var Q13;
            {var subQ0=sQuery(id+"F0.wireOp",EDGE,"60ae7ea0-6620-475c-871b-af027508dd5f0.MirrorC");var subQ1=sQuery(id+"F0.wireOp",EDGE,"E4");var subQ2=makeQuery(id+"F0.imprint","INTERSECT",VERTEX,{"disambiguationData":[OD(0.0)],"derivedFrom":[subQ1,subQ0]});Q13=makeQuery(id+"F0.imprint","IMPRINT",FACE,{"disambiguationData":[TD([[makeQuery(id+"F0.imprint","IMPRINT",EDGE,{"disambiguationData":[TD([[subQ2,-1.0]])],"derivedFrom":subQ1}),1.0]])]});}
            var Q14;
            {var subQ0=sQuery(id+"F0.wireOp",EDGE,"1c631775-3706-4f81-9fae-aeb5620db3840.MirrorC");var subQ1=sQuery(id+"F0.wireOp",EDGE,"E4");var subQ2=makeQuery(id+"F0.imprint","INTERSECT",VERTEX,{"disambiguationData":[OD(0.0)],"derivedFrom":[subQ1,subQ0]});Q14=makeQuery(id+"F0.imprint","IMPRINT",FACE,{"disambiguationData":[TD([[makeQuery(id+"F0.imprint","IMPRINT",EDGE,{"disambiguationData":[TD([[subQ2,-1.0]])],"derivedFrom":subQ1}),-1.0]])]});}
            var Q15;
            {var subQ0=sQuery(id+"F0.wireOp",EDGE,"1c631775-3706-4f81-9fae-aeb5620db3840.MirrorC");var subQ1=sQuery(id+"F0.wireOp",EDGE,"E4");var subQ2=makeQuery(id+"F0.imprint","INTERSECT",VERTEX,{"disambiguationData":[OD(0.0)],"derivedFrom":[subQ1,subQ0]});Q15=makeQuery(id+"F0.imprint","IMPRINT",FACE,{"disambiguationData":[TD([[makeQuery(id+"F0.imprint","IMPRINT",EDGE,{"disambiguationData":[TD([[subQ2,-1.0]])],"derivedFrom":subQ1}),1.0]])]});}
            var Q16;
            {var subQ0=sQuery(id+"F0.wireOp",EDGE,"E4");var subQ1=sQuery(id+"F0.wireOp",EDGE,"E1");var subQ2=makeQuery(id+"F0.imprint","INTERSECT",VERTEX,{"disambiguationData":[OD(1.0)],"derivedFrom":[subQ1,subQ0]});Q16=makeQuery(id+"F0.imprint","IMPRINT",FACE,{"disambiguationData":[TD([[makeQuery(id+"F0.imprint","IMPRINT",EDGE,{"disambiguationData":[TD([[subQ2,-1.0]])],"derivedFrom":subQ1}),1.0]])]});}
            var Q17;
            {var subQ0=sQuery(id+"F0.wireOp",EDGE,"E5");var subQ1=sQuery(id+"F0.wireOp",EDGE,"E1");var subQ2=makeQuery(id+"F0.imprint","INTERSECT",VERTEX,{"disambiguationData":[OD(0.0)],"derivedFrom":[subQ1,subQ0]});Q17=makeQuery(id+"F0.imprint","IMPRINT",FACE,{"disambiguationData":[TD([[makeQuery(id+"F0.imprint","IMPRINT",EDGE,{"disambiguationData":[TD([[subQ2,-1.0]])],"derivedFrom":subQ1}),1.0]])]});}
            var Q18;
            {var subQ0=sQuery(id+"F0.wireOp",EDGE,"E4");var subQ1=sQuery(id+"F0.wireOp",EDGE,"E2");var subQ2=makeQuery(id+"F0.imprint","INTERSECT",VERTEX,{"disambiguationData":[OD(1.0)],"derivedFrom":[subQ1,subQ0]});Q18=makeQuery(id+"F0.imprint","IMPRINT",FACE,{"disambiguationData":[TD([[makeQuery(id+"F0.imprint","IMPRINT",EDGE,{"disambiguationData":[TD([[subQ2,-1.0]])],"derivedFrom":subQ1}),-1.0]])]});}
            var Q19;
            {var subQ0=sQuery(id+"F0.wireOp",EDGE,"E4");var subQ1=sQuery(id+"F0.wireOp",EDGE,"E2");var subQ2=makeQuery(id+"F0.imprint","INTERSECT",VERTEX,{"disambiguationData":[OD(1.0)],"derivedFrom":[subQ1,subQ0]});Q19=makeQuery(id+"F0.imprint","IMPRINT",FACE,{"disambiguationData":[TD([[makeQuery(id+"F0.imprint","IMPRINT",EDGE,{"disambiguationData":[TD([[subQ2,-1.0]])],"derivedFrom":subQ1}),1.0]])]});}
            var Q20;
            {var subQ0=sQuery(id+"F0.wireOp",EDGE,"E9.MirrorC");var subQ1=sQuery(id+"F0.wireOp",EDGE,"E2");var subQ2=makeQuery(id+"F0.imprint","INTERSECT",VERTEX,{"disambiguationData":[OD(0.0)],"derivedFrom":[subQ1,subQ0]});Q20=makeQuery(id+"F0.imprint","IMPRINT",FACE,{"disambiguationData":[TD([[makeQuery(id+"F0.imprint","IMPRINT",EDGE,{"disambiguationData":[TD([[subQ2,-1.0]])],"derivedFrom":subQ1}),1.0]])]});}
            var Q21;
            {var subQ0=sQuery(id+"F0.wireOp",EDGE,"E9.MirrorC");var subQ1=sQuery(id+"F0.wireOp",EDGE,"E2");var subQ2=makeQuery(id+"F0.imprint","INTERSECT",VERTEX,{"disambiguationData":[OD(0.0)],"derivedFrom":[subQ1,subQ0]});Q21=makeQuery(id+"F0.imprint","IMPRINT",FACE,{"disambiguationData":[TD([[makeQuery(id+"F0.imprint","IMPRINT",EDGE,{"disambiguationData":[TD([[subQ2,-1.0]])],"derivedFrom":subQ1}),-1.0]])]});}
            extrude(context, id + "F3", {"entities" : qUnion([Q0, Q1, Q2, Q3, Q4, Q5, Q6, Q7, Q8, Q9, Q10, Q11, Q12, Q13, Q14, Q15, Q16, Q17, Q18, Q19, Q20, Q21]), "operationType" : NewBodyOperationType.REMOVE, "depth" : 3 * mm});
        }
        {
            var Q0;
            Q0=makeQuery(id+"F1.opExtrude","CAP_FACE",FACE,{"disambiguationData":[OSD([sQuery(id+"F0.wireOp",EDGE,"E3"),sQuery(id+"F0.wireOp",EDGE,"E4"),sQuery(id+"F0.wireOp",EDGE,"E10"),sQuery(id+"F0.wireOp",EDGE,"E11"),sQuery(id+"F0.wireOp",EDGE,"E12"),sQuery(id+"F0.wireOp",EDGE,"E14.MirrorCS"),sQuery(id+"F0.wireOp",EDGE,"E15.MirrorCS"),sQuery(id+"F0.wireOp",EDGE,"E16.MirrorCS")])],"isStart":false});
            var sketch = newSketch(context, id + "F4", { "sketchPlane" : qUnion([Q0])});
            skLineSegment(sketch, "E17", {"start": v(-7.76, -7.76) * mm, "end": v(7.76, 7.76) * mm});
            skLineSegment(sketch, "E18", {"start": v(-10.78, 10.78) * mm, "end": v(10.78, -10.78) * mm});
            skLineSegment(sketch, "E19", {"start": v(-6.54, 6.54) * mm, "end": v(-4.05, 9.03) * mm});
            skLineSegment(sketch, "E20", {"start": v(-4.05, 9.03) * mm, "end": v(-6.67, 11.65) * mm});
            skLineSegment(sketch, "E21", {"start": v(-6.67, 11.65) * mm, "end": v(-9.16, 9.16) * mm});
            skLineSegment(sketch, "E22.MirrorCS", {"start": v(-11.65, 6.67) * mm, "end": v(-9.16, 9.16) * mm});
            skLineSegment(sketch, "E23.MirrorCS", {"start": v(-6.54, 6.54) * mm, "end": v(-9.03, 4.05) * mm});
            skLineSegment(sketch, "E24.MirrorCS", {"start": v(-9.03, 4.05) * mm, "end": v(-11.65, 6.67) * mm});
            skLineSegment(sketch, "E25.MirrorCS", {"start": v(6.54, -6.54) * mm, "end": v(9.03, -4.05) * mm});
            skLineSegment(sketch, "E26.MirrorCS", {"start": v(9.03, -4.05) * mm, "end": v(11.65, -6.67) * mm});
            skLineSegment(sketch, "E27.MirrorCS", {"start": v(11.65, -6.67) * mm, "end": v(9.16, -9.16) * mm});
            skLineSegment(sketch, "E28.MirrorCS", {"start": v(6.67, -11.65) * mm, "end": v(9.16, -9.16) * mm});
            skLineSegment(sketch, "E29.MirrorCS", {"start": v(6.54, -6.54) * mm, "end": v(4.05, -9.03) * mm});
            skLineSegment(sketch, "E30.MirrorCS", {"start": v(4.05, -9.03) * mm, "end": v(6.67, -11.65) * mm});
            skSolve(sketch);
        }
        {
            var Q0;
            Q0 = qSketchRegion(id + "F4", true);
            extrude(context, id + "F5", {"entities" : qUnion([Q0]), "operationType" : NewBodyOperationType.REMOVE, "oppositeDirection" : true, "depth" : 10 * mm});
        }
        {
            var Q0;
            Q0=makeQuery(id+"F5.boolean.opBoolean","COPY",EDGE,{"derivedFrom":makeQuery(id+"F5.opExtrude","CAP_EDGE",EDGE,{"disambiguationData":[OSD([sQuery(id+"F4.wireOp",EDGE,"E26.MirrorCS")])],"isStart":false})});
            var Q1;
            Q1=makeQuery(id+"F5.boolean.opBoolean","COPY",EDGE,{"derivedFrom":makeQuery(id+"F5.opExtrude","CAP_EDGE",EDGE,{"disambiguationData":[OSD([sQuery(id+"F4.wireOp",EDGE,"E30.MirrorCS")])],"isStart":false})});
            chamfer(context, id + "F6", {"entities" : qUnion([Q0, Q1]), "chamferType" : ChamferType.OFFSET_ANGLE, "width" : 2.1 * mm, "oppositeDirection" : false, "angle" : 60 * degree});
        }
        {
            var Q0;
            Q0=makeQuery(id+"F5.boolean.opBoolean","COPY",EDGE,{"derivedFrom":makeQuery(id+"F5.opExtrude","CAP_EDGE",EDGE,{"disambiguationData":[OSD([sQuery(id+"F4.wireOp",EDGE,"E20")])],"isStart":false})});
            var Q1;
            Q1=makeQuery(id+"F5.boolean.opBoolean","COPY",EDGE,{"derivedFrom":makeQuery(id+"F5.opExtrude","CAP_EDGE",EDGE,{"disambiguationData":[OSD([sQuery(id+"F4.wireOp",EDGE,"E24.MirrorCS")])],"isStart":false})});
            chamfer(context, id + "F7", {"entities" : qUnion([Q0, Q1]), "chamferType" : ChamferType.OFFSET_ANGLE, "width" : 2.1 * mm, "oppositeDirection" : true, "angle" : 60 * degree, "tangentPropagation" : true});
        }
        {
            var Q0;
            Q0=makeQuery(id+"F5.boolean.opBoolean","COPY",FACE,{"derivedFrom":makeQuery(id+"F5.opExtrude","SWEPT_FACE",FACE,{"disambiguationData":[OSD([sQuery(id+"F4.wireOp",EDGE,"E25.MirrorCS"),sQuery(id+"F4.wireOp",EDGE,"E29.MirrorCS")])]})});
            var sketch = newSketch(context, id + "F8", { "sketchPlane" : qUnion([Q0])});
            skCircle(sketch, "E31.cCircle", {"center": v(0, 14.13) * mm, "radius": 3.52 * mm, "construction": true});
            skPoint(sketch, "E31.cCircle.perimeterSnap0", {"position": v(-1.76, 11.08) * mm});
            skLineSegment(sketch, "E31.0", {"start": v(0, 10.07) * mm, "end": v(-3.52, 12.1) * mm});
            skLineSegment(sketch, "E31.1", {"start": v(-3.52, 12.1) * mm, "end": v(-3.52, 16.16) * mm});
            skLineSegment(sketch, "E31.2", {"start": v(-3.52, 16.16) * mm, "end": v(0, 18.2) * mm});
            skLineSegment(sketch, "E31.3", {"start": v(0, 18.2) * mm, "end": v(3.52, 16.16) * mm});
            skLineSegment(sketch, "E31.4", {"start": v(3.52, 16.16) * mm, "end": v(3.52, 12.1) * mm});
            skLineSegment(sketch, "E31.5", {"start": v(3.52, 12.1) * mm, "end": v(0, 10.07) * mm});
            skPoint(sketch, "E31.0.midPoint", {"position": v(-1.76, 11.08) * mm});
            skPoint(sketch, "E31.0.midPoint.positionSnap0", {"position": v(-1.76, 11.08) * mm});
            skCircle(sketch, "E32", {"center": v(0, 14.13) * mm, "radius": 2 * mm});
            skSolve(sketch);
        }
        {
            var Q0;
            Q0=makeQuery(id+"F8.imprint","IMPRINT",FACE,{"disambiguationData":[TD([[makeQuery(id+"F8.imprint","IMPRINT",EDGE,{"derivedFrom":sQuery(id+"F8.wireOp",EDGE,"E32")}),1.0]])]});
            extrude(context, id + "F9", {"entities" : qUnion([Q0]), "operationType" : NewBodyOperationType.REMOVE, "depth" : 6 * mm});
        }
        {
            var Q0;
            Q0=makeQuery(id+"F8.imprint","IMPRINT",FACE,{"disambiguationData":[TD([[makeQuery(id+"F8.imprint","IMPRINT",EDGE,{"derivedFrom":sQuery(id+"F8.wireOp",EDGE,"E32")}),1.0]])]});
            extrude(context, id + "F10", {"entities" : qUnion([Q0]), "operationType" : NewBodyOperationType.REMOVE, "oppositeDirection" : true, "depth" : 24.5 * mm});
        }
    });
